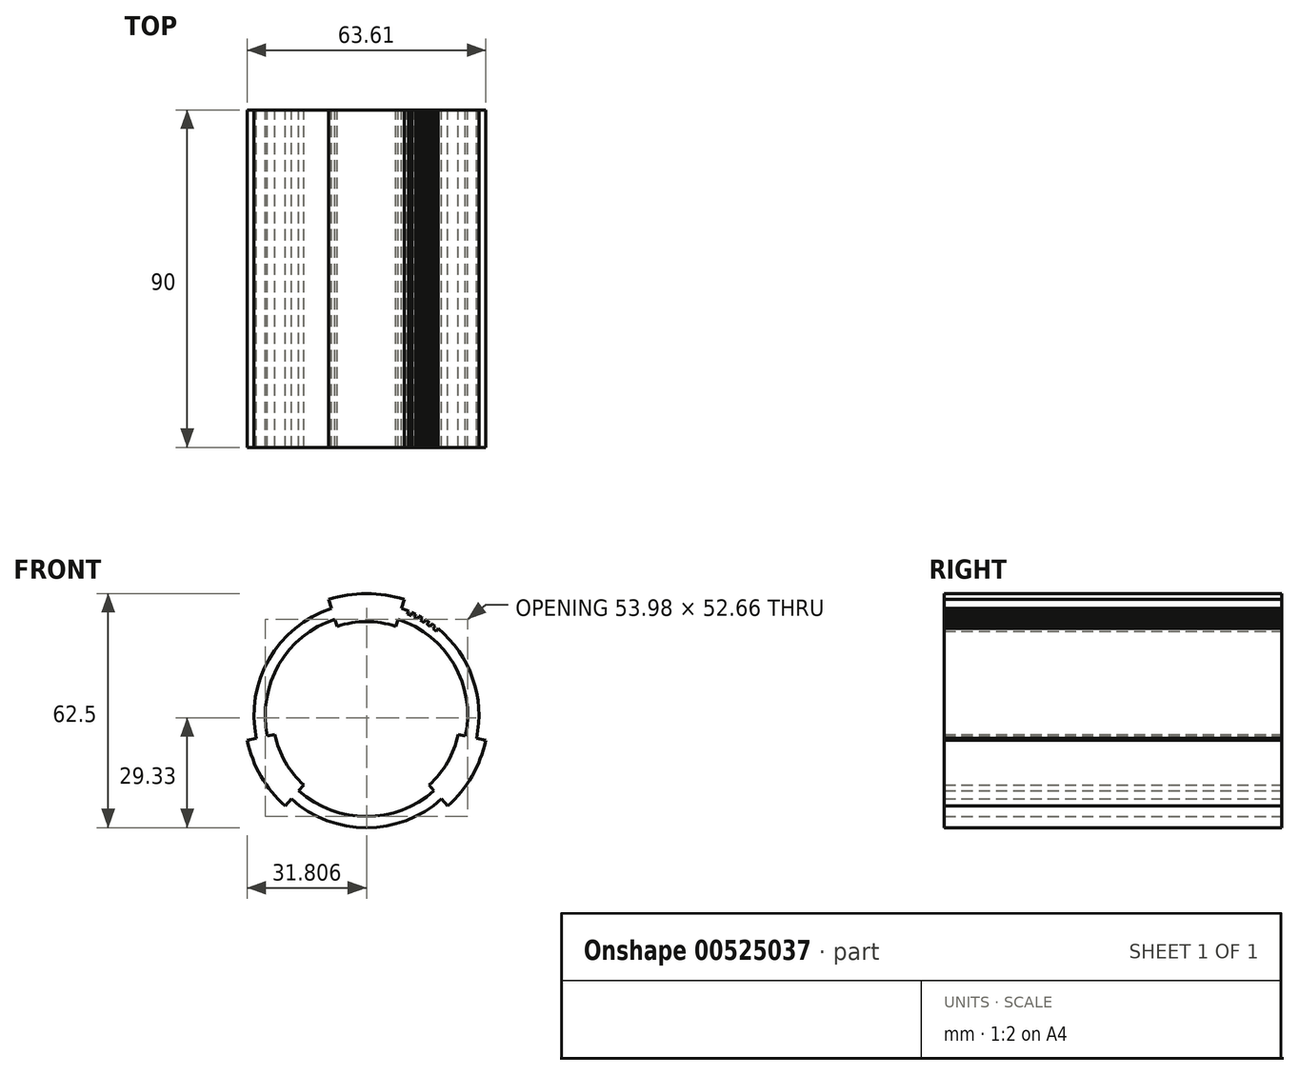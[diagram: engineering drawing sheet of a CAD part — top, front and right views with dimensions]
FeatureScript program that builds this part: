
annotation { "Feature Type Name" : "Feature", "Feature Type Description" : "" }
export const myFeature = defineFeature(function(context is Context, id is Id, definition is map)
    precondition{}
    {
        {
            var Q0;
            Q0=qCreatedBy(makeId("Front.planeOp"),FACE);
            var sketch = newSketch(context, id + "F0", { "sketchPlane" : qUnion([Q0])});
            skArc(sketch, "E0", {"start": v(-14.55, 20.43) * mm, "mid": v(-31.2, 6.92) * mm, "end": v(-34.58, -14.27) * mm});
            skArc(sketch, "E1.0", {"start": v(-13.61, 17.58) * mm, "mid": v(-28.6, 5.42) * mm, "end": v(-31.64, -13.65) * mm});
            skLineSegment(sketch, "E2", {"start": v(-13, 15.68) * mm, "end": v(-13.61, 17.58) * mm});
            skLineSegment(sketch, "E3.MirrorCS", {"start": v(2.54, 15.68) * mm, "end": v(3.17, 17.58) * mm});
            skArc(sketch, "E4.trimOffspring", {"start": v(4.87, 22.8) * mm, "mid": v(-5.22, 24.42) * mm, "end": v(-15.32, 22.8) * mm});
            skArc(sketch, "E5.trimOffspring", {"start": v(2.54, 15.68) * mm, "mid": v(-5.22, 16.92) * mm, "end": v(-13, 15.68) * mm});
            skPoint(sketch, "E6.start.orphan", {"position": v(-15.32, -38.97) * mm});
            skPoint(sketch, "E7.trimOffspring.end.orphan", {"position": v(4.87, -38.97) * mm});
            skLineSegment(sketch, "E8.trimOffspring", {"start": v(-14.55, 20.43) * mm, "end": v(-15.32, 22.8) * mm});
            skLineSegment(sketch, "E9.trimOffspring", {"start": v(4.1, 20.43) * mm, "end": v(4.87, 22.8) * mm});
            skLineSegment(sketch, "E10", {"start": v(-5.22, -8.08) * mm, "end": v(-5.22, 24.42) * mm});
            skArc(sketch, "E11.1.0", {"start": v(-37.03, -14.78) * mm, "mid": v(-33.37, -24.33) * mm, "end": v(-26.93, -32.27) * mm});
            skArc(sketch, "E11.1.1", {"start": v(-29.69, -13.23) * mm, "mid": v(-26.88, -20.58) * mm, "end": v(-21.92, -26.7) * mm});
            skLineSegment(sketch, "E11.1.2", {"start": v(-25.26, -30.41) * mm, "end": v(-26.93, -32.27) * mm});
            skLineSegment(sketch, "E11.1.3", {"start": v(-21.92, -26.7) * mm, "end": v(-23.25, -28.18) * mm});
            skLineSegment(sketch, "E11.1.4", {"start": v(-29.69, -13.23) * mm, "end": v(-31.64, -13.65) * mm});
            skLineSegment(sketch, "E11.1.5", {"start": v(-34.58, -14.27) * mm, "end": v(-37.03, -14.78) * mm});
            skArc(sketch, "E11.2.0", {"start": v(16.48, -32.27) * mm, "mid": v(22.92, -24.33) * mm, "end": v(26.58, -14.78) * mm});
            skArc(sketch, "E11.2.1", {"start": v(11.47, -26.7) * mm, "mid": v(16.43, -20.58) * mm, "end": v(19.24, -13.23) * mm});
            skLineSegment(sketch, "E11.2.2", {"start": v(24.13, -14.27) * mm, "end": v(26.58, -14.78) * mm});
            skLineSegment(sketch, "E11.2.3", {"start": v(19.24, -13.23) * mm, "end": v(21.2, -13.65) * mm});
            skLineSegment(sketch, "E11.2.4", {"start": v(11.47, -26.7) * mm, "end": v(12.8, -28.18) * mm});
            skLineSegment(sketch, "E11.2.5", {"start": v(14.8, -30.41) * mm, "end": v(16.48, -32.27) * mm});
            skArc(sketch, "E12.trimOffspring", {"start": v(21.2, -13.65) * mm, "mid": v(18.16, 5.42) * mm, "end": v(3.17, 17.58) * mm});
            skArc(sketch, "E13.trimOffspring", {"start": v(24.13, -14.27) * mm, "mid": v(23.1, 1.83) * mm, "end": v(13.87, 15.06) * mm});
            skArc(sketch, "E14.trimOffspring", {"start": v(-23.25, -28.18) * mm, "mid": v(-5.22, -35.08) * mm, "end": v(12.8, -28.18) * mm});
            skArc(sketch, "E15.trimOffspring", {"start": v(-25.26, -30.41) * mm, "mid": v(-5.22, -38.08) * mm, "end": v(14.8, -30.41) * mm});
            skLineSegment(sketch, "E16", {"start": v(5.68, 18.96) * mm, "end": v(6, 19.74) * mm});
            skLineSegment(sketch, "E17.1.0", {"start": v(6.6, 18.57) * mm, "end": v(6.94, 19.34) * mm});
            skLineSegment(sketch, "E17.2.0", {"start": v(7.5, 18.15) * mm, "end": v(7.86, 18.91) * mm});
            skLineSegment(sketch, "E17.3.0", {"start": v(8.38, 17.7) * mm, "end": v(8.77, 18.45) * mm});
            skLineSegment(sketch, "E17.4.0", {"start": v(9.25, 17.22) * mm, "end": v(9.67, 17.96) * mm});
            skLineSegment(sketch, "E17.5.0", {"start": v(10.1, 16.72) * mm, "end": v(10.55, 17.44) * mm});
            skLineSegment(sketch, "E17.6.0", {"start": v(10.94, 16.18) * mm, "end": v(11.4, 16.89) * mm});
            skLineSegment(sketch, "E17.7.0", {"start": v(11.75, 15.62) * mm, "end": v(12.25, 16.3) * mm});
            skLineSegment(sketch, "E17.8.0", {"start": v(12.55, 15.02) * mm, "end": v(13.07, 15.7) * mm});
            skLineSegment(sketch, "E17.9.0", {"start": v(13.33, 14.4) * mm, "end": v(13.87, 15.06) * mm});
            skLineSegment(sketch, "E17.anchor1", {"start": v(5.68, 18.96) * mm, "end": v(6, 19.74) * mm, "construction": true});
            skLineSegment(sketch, "E17.anchor2", {"start": v(13.33, 14.4) * mm, "end": v(13.87, 15.06) * mm, "construction": true});
            skArc(sketch, "E18", {"start": v(13.33, 14.4) * mm, "mid": v(12.94, 14.72) * mm, "end": v(12.55, 15.02) * mm});
            skArc(sketch, "E19.trimOffspring", {"start": v(6.6, 18.57) * mm, "mid": v(6.14, 18.77) * mm, "end": v(5.68, 18.96) * mm});
            skArc(sketch, "E20.trimOffspring", {"start": v(8.38, 17.7) * mm, "mid": v(7.94, 17.93) * mm, "end": v(7.5, 18.15) * mm});
            skArc(sketch, "E21.trimOffspring", {"start": v(10.1, 16.72) * mm, "mid": v(9.68, 16.97) * mm, "end": v(9.25, 17.22) * mm});
            skArc(sketch, "E22.trimOffspring", {"start": v(11.75, 15.62) * mm, "mid": v(11.35, 15.9) * mm, "end": v(10.94, 16.18) * mm});
            skArc(sketch, "E23.trimOffspring", {"start": v(6, 19.74) * mm, "mid": v(5.05, 20.1) * mm, "end": v(4.1, 20.43) * mm});
            skArc(sketch, "E24.trimOffspring", {"start": v(7.86, 18.91) * mm, "mid": v(7.4, 19.13) * mm, "end": v(6.94, 19.34) * mm});
            skArc(sketch, "E25.trimOffspring", {"start": v(9.67, 17.96) * mm, "mid": v(9.22, 18.21) * mm, "end": v(8.77, 18.45) * mm});
            skArc(sketch, "E26.trimOffspring", {"start": v(11.4, 16.89) * mm, "mid": v(10.98, 17.17) * mm, "end": v(10.55, 17.44) * mm});
            skArc(sketch, "E27.trimOffspring", {"start": v(13.07, 15.7) * mm, "mid": v(12.66, 16) * mm, "end": v(12.25, 16.3) * mm});
            skSolve(sketch);
        }
        {
            var Q0;
            Q0=makeQuery(id+"F0.imprint","IMPRINT",FACE,{"disambiguationData":[TD([[makeQuery(id+"F0.imprint","IMPRINT",EDGE,{"derivedFrom":sQuery(id+"F0.wireOp",EDGE,"E0")}),1.0]])]});
            extrude(context, id + "F1", {"entities" : qUnion([Q0]), "depth" : 90 * mm, "offsetDistance" : 25 * mm});
        }
    });
